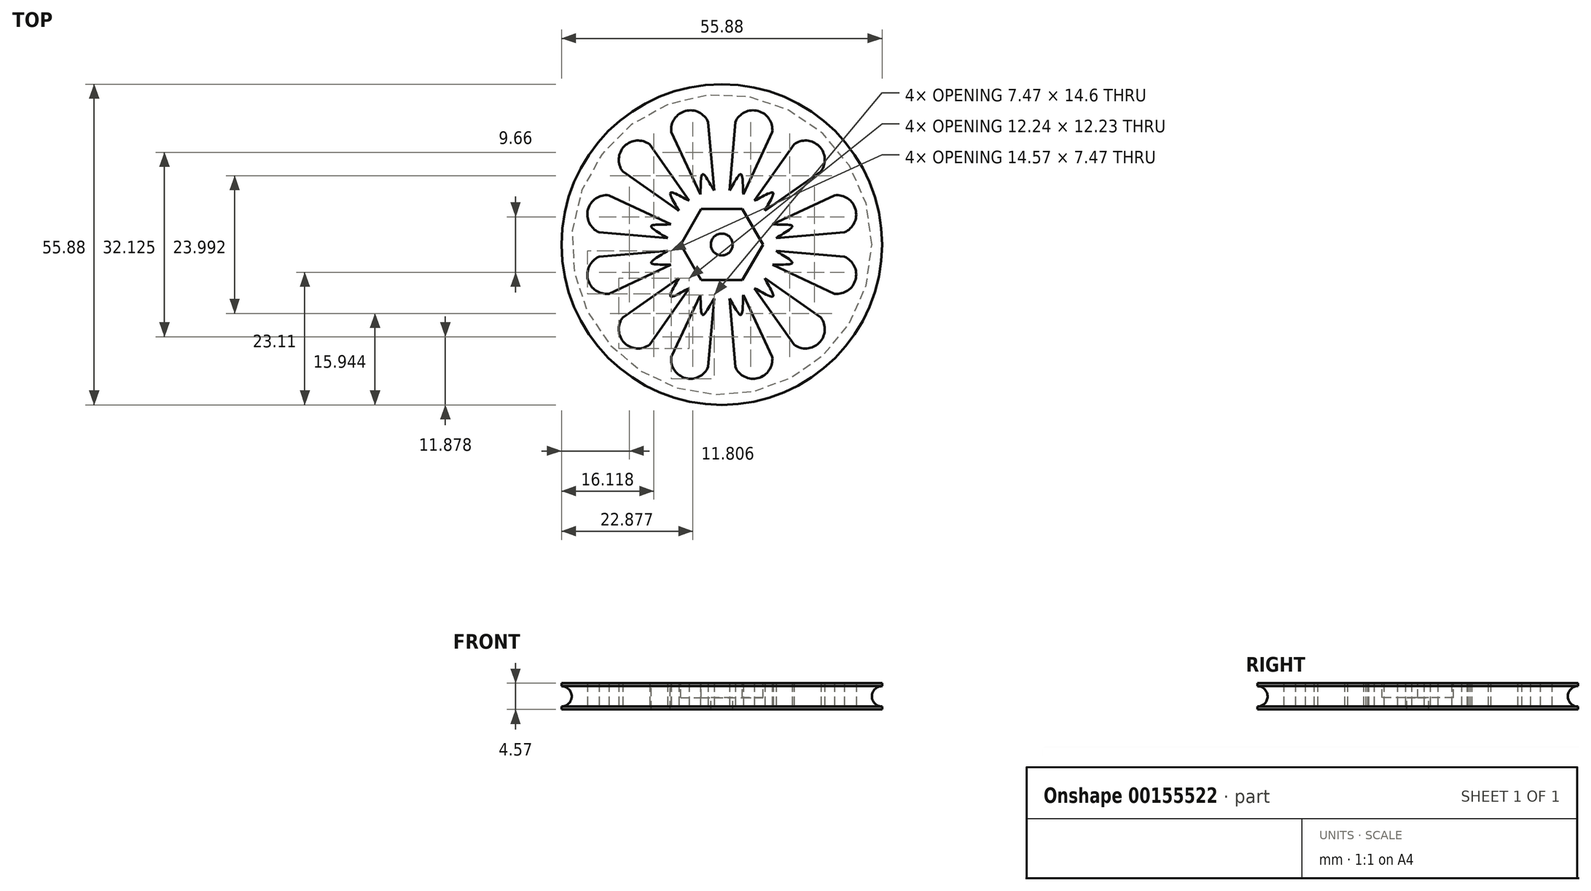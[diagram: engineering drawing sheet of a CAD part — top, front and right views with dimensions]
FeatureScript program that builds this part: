
annotation { "Feature Type Name" : "Feature", "Feature Type Description" : "" }
export const myFeature = defineFeature(function(context is Context, id is Id, definition is map)
    precondition{}
    {
        {
            var Q0;
            Q0=qCreatedBy(makeId("Top.planeOp"),FACE);
            var sketch = newSketch(context, id + "F0", { "sketchPlane" : qUnion([Q0])});
            skCircle(sketch, "E0", {"center": v(0, 0) * mm, "radius": 27.94 * mm});
            skLineSegment(sketch, "E1", {"start": v(-27.94, 0) * mm, "end": v(27.94, 0) * mm, "construction": true});
            skLineSegment(sketch, "E2", {"start": v(0, -27.94) * mm, "end": v(0, 27.94) * mm, "construction": true});
            skArc(sketch, "E3", {"start": v(2.37, 21.33) * mm, "mid": v(6.33, 23.27) * mm, "end": v(8.8, 19.6) * mm});
            skArc(sketch, "E4", {"start": v(12.57, 17.44) * mm, "mid": v(16.97, 17.13) * mm, "end": v(17.27, 12.73) * mm});
            skArc(sketch, "E5", {"start": v(19.67, 8.57) * mm, "mid": v(23.32, 6.1) * mm, "end": v(21.39, 2.14) * mm});
            skArc(sketch, "E6.MirrorCS", {"start": v(-2.37, 21.33) * mm, "mid": v(-6.33, 23.27) * mm, "end": v(-8.8, 19.6) * mm});
            skArc(sketch, "E7.MirrorCS", {"start": v(-12.57, 17.44) * mm, "mid": v(-16.97, 17.13) * mm, "end": v(-17.27, 12.73) * mm});
            skArc(sketch, "E8.MirrorCS", {"start": v(-19.67, 8.57) * mm, "mid": v(-23.32, 6.1) * mm, "end": v(-21.39, 2.14) * mm});
            skArc(sketch, "E9.MirrorCS", {"start": v(-19.67, -8.57) * mm, "mid": v(-23.32, -6.1) * mm, "end": v(-21.39, -2.14) * mm});
            skArc(sketch, "E10.MirrorCS", {"start": v(-12.57, -17.44) * mm, "mid": v(-16.97, -17.13) * mm, "end": v(-17.27, -12.73) * mm});
            skArc(sketch, "E11.MirrorCS", {"start": v(-2.37, -21.33) * mm, "mid": v(-6.33, -23.27) * mm, "end": v(-8.8, -19.6) * mm});
            skArc(sketch, "E12.MirrorCS", {"start": v(2.37, -21.33) * mm, "mid": v(6.33, -23.27) * mm, "end": v(8.8, -19.6) * mm});
            skArc(sketch, "E13.MirrorCS", {"start": v(12.57, -17.44) * mm, "mid": v(16.97, -17.13) * mm, "end": v(17.27, -12.73) * mm});
            skArc(sketch, "E14.MirrorCS", {"start": v(19.67, -8.57) * mm, "mid": v(23.32, -6.1) * mm, "end": v(21.39, -2.14) * mm});
            skCircle(sketch, "E15", {"center": v(0, 0) * mm, "radius": 6.99 * mm, "construction": true});
            skLineSegment(sketch, "E16.0", {"start": v(6.99, 0) * mm, "end": v(3.5, -6.05) * mm});
            skLineSegment(sketch, "E16.1", {"start": v(3.5, -6.05) * mm, "end": v(-3.5, -6.05) * mm});
            skLineSegment(sketch, "E16.2", {"start": v(-3.5, -6.05) * mm, "end": v(-6.99, 0) * mm});
            skLineSegment(sketch, "E16.3", {"start": v(-6.99, 0) * mm, "end": v(-3.5, 6.05) * mm});
            skLineSegment(sketch, "E16.4", {"start": v(-3.5, 6.05) * mm, "end": v(3.5, 6.05) * mm});
            skLineSegment(sketch, "E16.5", {"start": v(3.5, 6.05) * mm, "end": v(6.99, 0) * mm});
            skCircle(sketch, "E17", {"center": v(0, 0) * mm, "radius": 9.53 * mm, "construction": true});
            skLineSegment(sketch, "E18.trimOffspring", {"start": v(-3.74, 8.76) * mm, "end": v(-8.8, 19.6) * mm});
            skLineSegment(sketch, "E19.trimOffspring", {"start": v(-5.7, 7.63) * mm, "end": v(-12.57, 17.44) * mm});
            skLineSegment(sketch, "E20.trimOffspring", {"start": v(-7.5, 5.88) * mm, "end": v(-17.27, 12.73) * mm});
            skLineSegment(sketch, "E21.trimOffspring", {"start": v(-8.85, 3.52) * mm, "end": v(-19.67, 8.57) * mm});
            skLineSegment(sketch, "E22.trimOffspring", {"start": v(-9.46, 1.1) * mm, "end": v(-21.39, 2.14) * mm});
            skLineSegment(sketch, "E23.trimOffspring", {"start": v(-9.46, -1.1) * mm, "end": v(-21.39, -2.14) * mm});
            skLineSegment(sketch, "E24.trimOffspring", {"start": v(-8.85, -3.52) * mm, "end": v(-19.67, -8.57) * mm});
            skLineSegment(sketch, "E25.trimOffspring", {"start": v(-7.5, -5.88) * mm, "end": v(-17.27, -12.73) * mm});
            skLineSegment(sketch, "E26.trimOffspring", {"start": v(-5.7, -7.63) * mm, "end": v(-12.57, -17.44) * mm});
            skLineSegment(sketch, "E27.trimOffspring", {"start": v(-3.74, -8.76) * mm, "end": v(-8.8, -19.6) * mm});
            skLineSegment(sketch, "E28.trimOffspring", {"start": v(-1.33, -9.43) * mm, "end": v(-2.37, -21.33) * mm});
            skLineSegment(sketch, "E29.trimOffspring", {"start": v(1.33, -9.43) * mm, "end": v(2.37, -21.33) * mm});
            skLineSegment(sketch, "E30.trimOffspring", {"start": v(3.74, -8.76) * mm, "end": v(8.8, -19.6) * mm});
            skLineSegment(sketch, "E31.trimOffspring", {"start": v(5.7, -7.63) * mm, "end": v(12.57, -17.44) * mm});
            skLineSegment(sketch, "E32.trimOffspring", {"start": v(7.5, -5.88) * mm, "end": v(17.27, -12.73) * mm});
            skLineSegment(sketch, "E33.trimOffspring", {"start": v(8.85, -3.52) * mm, "end": v(19.67, -8.57) * mm});
            skLineSegment(sketch, "E34.trimOffspring", {"start": v(9.46, -1.1) * mm, "end": v(21.39, -2.14) * mm});
            skLineSegment(sketch, "E35.trimOffspring", {"start": v(9.46, 1.1) * mm, "end": v(21.39, 2.14) * mm});
            skLineSegment(sketch, "E36.trimOffspring", {"start": v(8.85, 3.52) * mm, "end": v(19.67, 8.57) * mm});
            skLineSegment(sketch, "E37.trimOffspring", {"start": v(7.5, 5.88) * mm, "end": v(17.27, 12.73) * mm});
            skLineSegment(sketch, "E38.trimOffspring", {"start": v(5.7, 7.63) * mm, "end": v(12.57, 17.44) * mm});
            skLineSegment(sketch, "E39.trimOffspring", {"start": v(3.74, 8.76) * mm, "end": v(8.8, 19.6) * mm});
            skLineSegment(sketch, "E40.trimOffspring", {"start": v(1.33, 9.43) * mm, "end": v(2.37, 21.33) * mm});
            skLineSegment(sketch, "E41.trimOffspring", {"start": v(-1.33, 9.43) * mm, "end": v(-2.37, 21.33) * mm});
            skLineSegment(sketch, "E42", {"start": v(5.46, 20.02) * mm, "end": v(0, 0) * mm, "construction": true});
            skLineSegment(sketch, "E43", {"start": v(0, 0) * mm, "end": v(14.6, 14.76) * mm, "construction": true});
            skLineSegment(sketch, "E44", {"start": v(20.07, 5.23) * mm, "end": v(0, 0) * mm, "construction": true});
            skCircle(sketch, "E45", {"center": v(0, 0) * mm, "radius": 12.7 * mm, "construction": true});
            skFitSpline(sketch, "E46", {"points": [v(1.33, 9.43) * mm, v(3.34, 12.25) * mm, v(3.74, 8.76) * mm], "startDerivative": vector(4.33, 6.63) * mm, "endDerivative": vector(0.64, -7.98) * mm});
            skFitSpline(sketch, "E47", {"points": [v(5.7, 7.63) * mm, v(8.93, 9.03) * mm, v(7.5, 5.88) * mm], "startDerivative": vector(7.24, 3.44) * mm, "endDerivative": vector(-3.58, -7.06) * mm});
            skFitSpline(sketch, "E48", {"points": [v(8.85, 3.52) * mm, v(12.29, 3.2) * mm, v(9.46, 1.1) * mm], "startDerivative": vector(7.9, -0.42) * mm, "endDerivative": vector(-6.6, -4.55) * mm});
            skFitSpline(sketch, "E49.MirrorCS", {"points": [v(-1.33, 9.43) * mm, v(-3.34, 12.25) * mm, v(-3.74, 8.76) * mm], "startDerivative": vector(-4.33, 6.63) * mm, "endDerivative": vector(-0.64, -7.98) * mm});
            skFitSpline(sketch, "E50.MirrorCS", {"points": [v(-5.7, 7.63) * mm, v(-8.93, 9.03) * mm, v(-7.5, 5.88) * mm], "startDerivative": vector(-7.24, 3.44) * mm, "endDerivative": vector(3.58, -7.06) * mm});
            skFitSpline(sketch, "E51.MirrorCS", {"points": [v(-8.85, 3.52) * mm, v(-12.29, 3.2) * mm, v(-9.46, 1.1) * mm], "startDerivative": vector(-7.9, -0.42) * mm, "endDerivative": vector(6.6, -4.55) * mm});
            skFitSpline(sketch, "E52.MirrorCS", {"points": [v(-8.85, -3.52) * mm, v(-12.29, -3.2) * mm, v(-9.46, -1.1) * mm], "startDerivative": vector(-7.9, 0.42) * mm, "endDerivative": vector(6.6, 4.55) * mm});
            skFitSpline(sketch, "E53.MirrorCS", {"points": [v(-5.7, -7.63) * mm, v(-8.93, -9.03) * mm, v(-7.5, -5.88) * mm], "startDerivative": vector(-7.24, -3.44) * mm, "endDerivative": vector(3.58, 7.06) * mm});
            skFitSpline(sketch, "E54.MirrorCS", {"points": [v(-1.33, -9.43) * mm, v(-3.34, -12.25) * mm, v(-3.74, -8.76) * mm], "startDerivative": vector(-4.33, -6.63) * mm, "endDerivative": vector(-0.64, 7.98) * mm});
            skFitSpline(sketch, "E55.MirrorCS", {"points": [v(1.33, -9.43) * mm, v(3.34, -12.25) * mm, v(3.74, -8.76) * mm], "startDerivative": vector(4.33, -6.63) * mm, "endDerivative": vector(0.64, 7.98) * mm});
            skFitSpline(sketch, "E56.MirrorCS", {"points": [v(5.7, -7.63) * mm, v(8.93, -9.03) * mm, v(7.5, -5.88) * mm], "startDerivative": vector(7.24, -3.44) * mm, "endDerivative": vector(-3.58, 7.06) * mm});
            skFitSpline(sketch, "E57.MirrorCS", {"points": [v(8.85, -3.52) * mm, v(12.29, -3.2) * mm, v(9.46, -1.1) * mm], "startDerivative": vector(7.9, 0.42) * mm, "endDerivative": vector(-6.6, 4.55) * mm});
            skSolve(sketch);
        }
        {
            var Q0;
            Q0=makeQuery(id+"F0.imprint","IMPRINT",FACE,{"disambiguationData":[TD([[makeQuery(id+"F0.imprint","IMPRINT",EDGE,{"derivedFrom":sQuery(id+"F0.wireOp",EDGE,"E0")}),1.0]])]});
            var Q1;
            {var subQ0=sQuery(id+"F0.wireOp",EDGE,"E17");var subQ10=makeQuery(id+"F0.imprint","INTERSECT",VERTEX,{"derivedFrom":[subQ0,sQuery(id+"F0.wireOp",EDGE,"E35.trimOffspring")]});Q1=makeQuery(id+"F0.imprint","IMPRINT",FACE,{"disambiguationData":[TD([[makeQuery(id+"F0.imprint","IMPRINT",EDGE,{"disambiguationData":[TD([[subQ10,-1.0]])],"derivedFrom":subQ0}),1.0]])]});}
            var Q2;
            {var subQ0=sQuery(id+"F0.wireOp",EDGE,"E16.3");Q2=makeQuery(id+"F0.imprint","IMPRINT",FACE,{"disambiguationData":[TD([[makeQuery(id+"F0.imprint","IMPRINT",EDGE,{"derivedFrom":subQ0}),1.0]])]});}
            var Q3;
            {var subQ0=sQuery(id+"F0.wireOp",EDGE,"E16.2");Q3=makeQuery(id+"F0.imprint","IMPRINT",FACE,{"disambiguationData":[TD([[makeQuery(id+"F0.imprint","IMPRINT",EDGE,{"derivedFrom":subQ0}),1.0]])]});}
            var Q4;
            {var subQ0=sQuery(id+"F0.wireOp",EDGE,"E16.4");Q4=makeQuery(id+"F0.imprint","IMPRINT",FACE,{"disambiguationData":[TD([[makeQuery(id+"F0.imprint","IMPRINT",EDGE,{"derivedFrom":subQ0}),1.0]])]});}
            var Q5;
            {var subQ0=sQuery(id+"F0.wireOp",EDGE,"E16.5");Q5=makeQuery(id+"F0.imprint","IMPRINT",FACE,{"disambiguationData":[TD([[makeQuery(id+"F0.imprint","IMPRINT",EDGE,{"derivedFrom":subQ0}),1.0]])]});}
            var Q6;
            {var subQ0=sQuery(id+"F0.wireOp",EDGE,"E16.0");Q6=makeQuery(id+"F0.imprint","IMPRINT",FACE,{"disambiguationData":[TD([[makeQuery(id+"F0.imprint","IMPRINT",EDGE,{"derivedFrom":subQ0}),1.0]])]});}
            var Q7;
            {var subQ0=sQuery(id+"F0.wireOp",EDGE,"E16.1");Q7=makeQuery(id+"F0.imprint","IMPRINT",FACE,{"disambiguationData":[TD([[makeQuery(id+"F0.imprint","IMPRINT",EDGE,{"derivedFrom":subQ0}),1.0]])]});}
            var Q8;
            Q8=makeQuery(id+"F0.imprint","IMPRINT",FACE,{"disambiguationData":[TD([[makeQuery(id+"F0.imprint","IMPRINT",EDGE,{"derivedFrom":sQuery(id+"F0.wireOp",EDGE,"E16.0")}),-1.0]])]});
            extrude(context, id + "F1", {"entities" : qUnion([Q0, Q1, Q2, Q3, Q4, Q5, Q6, Q7, Q8]), "depth" : 4.57 * mm});
        }
        {
            var Q0;
            Q0=qCreatedBy(makeId("Front.planeOp"),FACE);
            var sketch = newSketch(context, id + "F2", { "sketchPlane" : qUnion([Q0])});
            skLineSegment(sketch, "E58", {"start": v(0, 0) * mm, "end": v(0, 4.57) * mm, "construction": true});
            skLineSegment(sketch, "E59", {"start": v(0, 0) * mm, "end": v(27.94, 0) * mm, "construction": true});
            skLineSegment(sketch, "E60", {"start": v(27.94, 0) * mm, "end": v(27.94, 4.57) * mm, "construction": true});
            skLineSegment(sketch, "E61", {"start": v(27.94, 4.57) * mm, "end": v(0, 4.57) * mm, "construction": true});
            skArc(sketch, "E62", {"start": v(27.94, 4.06) * mm, "mid": v(26.16, 2.29) * mm, "end": v(27.94, 0.5) * mm});
            skLineSegment(sketch, "E63", {"start": v(27.94, 4.06) * mm, "end": v(27.94, 0.5) * mm});
            skSolve(sketch);
        }
        {
            var Q0;
            Q0 = qSketchRegion(id + "F2", true);
            var Q1;
            Q1=sQuery(id+"F2.wireOp",EDGE,"E58");
            revolve(context, id + "F3", {"operationType" : NewBodyOperationType.REMOVE, "entities" : qUnion([Q0]), "axis" : qUnion([Q1]), "revolveType" : RevolveType.FULL, "oppositeDirection" : true});
        }
        {
            var Q0;
            Q0=makeQuery(id+"F1.opExtrude","CAP_FACE",FACE,{"disambiguationData":[OSD([sQuery(id+"F0.wireOp",EDGE,"E0"),sQuery(id+"F0.wireOp",EDGE,"E3"),sQuery(id+"F0.wireOp",EDGE,"E4"),sQuery(id+"F0.wireOp",EDGE,"E5"),sQuery(id+"F0.wireOp",EDGE,"E6.MirrorCS"),sQuery(id+"F0.wireOp",EDGE,"E7.MirrorCS"),sQuery(id+"F0.wireOp",EDGE,"E8.MirrorCS"),sQuery(id+"F0.wireOp",EDGE,"E9.MirrorCS"),sQuery(id+"F0.wireOp",EDGE,"E10.MirrorCS"),sQuery(id+"F0.wireOp",EDGE,"E11.MirrorCS"),sQuery(id+"F0.wireOp",EDGE,"E12.MirrorCS"),sQuery(id+"F0.wireOp",EDGE,"E13.MirrorCS"),sQuery(id+"F0.wireOp",EDGE,"E14.MirrorCS"),sQuery(id+"F0.wireOp",EDGE,"E18.trimOffspring"),sQuery(id+"F0.wireOp",EDGE,"E19.trimOffspring"),sQuery(id+"F0.wireOp",EDGE,"E20.trimOffspring"),sQuery(id+"F0.wireOp",EDGE,"E21.trimOffspring"),sQuery(id+"F0.wireOp",EDGE,"E22.trimOffspring"),sQuery(id+"F0.wireOp",EDGE,"E23.trimOffspring"),sQuery(id+"F0.wireOp",EDGE,"E24.trimOffspring"),sQuery(id+"F0.wireOp",EDGE,"E25.trimOffspring"),sQuery(id+"F0.wireOp",EDGE,"E26.trimOffspring"),sQuery(id+"F0.wireOp",EDGE,"E27.trimOffspring"),sQuery(id+"F0.wireOp",EDGE,"E28.trimOffspring"),sQuery(id+"F0.wireOp",EDGE,"E29.trimOffspring"),sQuery(id+"F0.wireOp",EDGE,"E30.trimOffspring"),sQuery(id+"F0.wireOp",EDGE,"E31.trimOffspring"),sQuery(id+"F0.wireOp",EDGE,"E32.trimOffspring"),sQuery(id+"F0.wireOp",EDGE,"E33.trimOffspring"),sQuery(id+"F0.wireOp",EDGE,"E34.trimOffspring"),sQuery(id+"F0.wireOp",EDGE,"E35.trimOffspring"),sQuery(id+"F0.wireOp",EDGE,"E36.trimOffspring"),sQuery(id+"F0.wireOp",EDGE,"E37.trimOffspring"),sQuery(id+"F0.wireOp",EDGE,"E38.trimOffspring"),sQuery(id+"F0.wireOp",EDGE,"E39.trimOffspring"),sQuery(id+"F0.wireOp",EDGE,"E40.trimOffspring"),sQuery(id+"F0.wireOp",EDGE,"E41.trimOffspring"),sQuery(id+"F0.wireOp",EDGE,"E46"),sQuery(id+"F0.wireOp",EDGE,"E47"),sQuery(id+"F0.wireOp",EDGE,"E48"),sQuery(id+"F0.wireOp",EDGE,"E49.MirrorCS"),sQuery(id+"F0.wireOp",EDGE,"E50.MirrorCS"),sQuery(id+"F0.wireOp",EDGE,"E51.MirrorCS"),sQuery(id+"F0.wireOp",EDGE,"E52.MirrorCS"),sQuery(id+"F0.wireOp",EDGE,"E53.MirrorCS"),sQuery(id+"F0.wireOp",EDGE,"E54.MirrorCS"),sQuery(id+"F0.wireOp",EDGE,"E55.MirrorCS"),sQuery(id+"F0.wireOp",EDGE,"E56.MirrorCS"),sQuery(id+"F0.wireOp",EDGE,"E57.MirrorCS")])],"isStart":false});
            var sketch = newSketch(context, id + "F4", { "sketchPlane" : qUnion([Q0])});
            skCircle(sketch, "E64", {"center": v(0, 0) * mm, "radius": 7.18 * mm, "construction": true});
            skLineSegment(sketch, "E65.0", {"start": v(7.18, 0) * mm, "end": v(3.59, -6.21) * mm});
            skLineSegment(sketch, "E65.1", {"start": v(3.59, -6.21) * mm, "end": v(-3.59, -6.21) * mm});
            skLineSegment(sketch, "E65.2", {"start": v(-3.59, -6.21) * mm, "end": v(-7.18, 0) * mm});
            skLineSegment(sketch, "E65.3", {"start": v(-7.18, 0) * mm, "end": v(-3.59, 6.21) * mm});
            skLineSegment(sketch, "E65.4", {"start": v(-3.59, 6.21) * mm, "end": v(3.59, 6.21) * mm});
            skLineSegment(sketch, "E65.5", {"start": v(3.59, 6.21) * mm, "end": v(7.18, 0) * mm});
            skSolve(sketch);
        }
        {
            var Q0;
            Q0 = qSketchRegion(id + "F4", true);
            extrude(context, id + "F5", {"entities" : qUnion([Q0]), "operationType" : NewBodyOperationType.REMOVE, "oppositeDirection" : true, "depth" : 2.54 * mm});
        }
        {
            var Q0;
            Q0=makeQuery(id+"F5.boolean.opBoolean","COPY",FACE,{"derivedFrom":makeQuery(id+"F5.opExtrude","CAP_FACE",FACE,{"disambiguationData":[OSD([sQuery(id+"F4.wireOp",EDGE,"E65.0"),sQuery(id+"F4.wireOp",EDGE,"E65.1"),sQuery(id+"F4.wireOp",EDGE,"E65.2"),sQuery(id+"F4.wireOp",EDGE,"E65.3"),sQuery(id+"F4.wireOp",EDGE,"E65.4"),sQuery(id+"F4.wireOp",EDGE,"E65.5")])],"isStart":false})});
            var sketch = newSketch(context, id + "F6", { "sketchPlane" : qUnion([Q0])});
            skPoint(sketch, "E66", {"position": v(0, 0) * mm});
            skSolve(sketch);
        }
        {
            var Q0;
            Q0=sQuery(id+"F6.wireOp",VERTEX,"E66");
            var Q1;
            Q1=makeQuery(id+"F1.opExtrude","SWEPT_BODY",BODY,{"disambiguationData":[OSD([sQuery(id+"F0.wireOp",EDGE,"E0"),sQuery(id+"F0.wireOp",EDGE,"E3"),sQuery(id+"F0.wireOp",EDGE,"E4"),sQuery(id+"F0.wireOp",EDGE,"E5"),sQuery(id+"F0.wireOp",EDGE,"E6.MirrorCS"),sQuery(id+"F0.wireOp",EDGE,"E7.MirrorCS"),sQuery(id+"F0.wireOp",EDGE,"E8.MirrorCS"),sQuery(id+"F0.wireOp",EDGE,"E9.MirrorCS"),sQuery(id+"F0.wireOp",EDGE,"E10.MirrorCS"),sQuery(id+"F0.wireOp",EDGE,"E11.MirrorCS"),sQuery(id+"F0.wireOp",EDGE,"E12.MirrorCS"),sQuery(id+"F0.wireOp",EDGE,"E13.MirrorCS"),sQuery(id+"F0.wireOp",EDGE,"E14.MirrorCS"),sQuery(id+"F0.wireOp",EDGE,"E18.trimOffspring"),sQuery(id+"F0.wireOp",EDGE,"E19.trimOffspring"),sQuery(id+"F0.wireOp",EDGE,"E20.trimOffspring"),sQuery(id+"F0.wireOp",EDGE,"E21.trimOffspring"),sQuery(id+"F0.wireOp",EDGE,"E22.trimOffspring"),sQuery(id+"F0.wireOp",EDGE,"E23.trimOffspring"),sQuery(id+"F0.wireOp",EDGE,"E24.trimOffspring"),sQuery(id+"F0.wireOp",EDGE,"E25.trimOffspring"),sQuery(id+"F0.wireOp",EDGE,"E26.trimOffspring"),sQuery(id+"F0.wireOp",EDGE,"E27.trimOffspring"),sQuery(id+"F0.wireOp",EDGE,"E28.trimOffspring"),sQuery(id+"F0.wireOp",EDGE,"E29.trimOffspring"),sQuery(id+"F0.wireOp",EDGE,"E30.trimOffspring"),sQuery(id+"F0.wireOp",EDGE,"E31.trimOffspring"),sQuery(id+"F0.wireOp",EDGE,"E32.trimOffspring"),sQuery(id+"F0.wireOp",EDGE,"E33.trimOffspring"),sQuery(id+"F0.wireOp",EDGE,"E34.trimOffspring"),sQuery(id+"F0.wireOp",EDGE,"E35.trimOffspring"),sQuery(id+"F0.wireOp",EDGE,"E36.trimOffspring"),sQuery(id+"F0.wireOp",EDGE,"E37.trimOffspring"),sQuery(id+"F0.wireOp",EDGE,"E38.trimOffspring"),sQuery(id+"F0.wireOp",EDGE,"E39.trimOffspring"),sQuery(id+"F0.wireOp",EDGE,"E40.trimOffspring"),sQuery(id+"F0.wireOp",EDGE,"E41.trimOffspring"),sQuery(id+"F0.wireOp",EDGE,"E46"),sQuery(id+"F0.wireOp",EDGE,"E47"),sQuery(id+"F0.wireOp",EDGE,"E48"),sQuery(id+"F0.wireOp",EDGE,"E49.MirrorCS"),sQuery(id+"F0.wireOp",EDGE,"E50.MirrorCS"),sQuery(id+"F0.wireOp",EDGE,"E51.MirrorCS"),sQuery(id+"F0.wireOp",EDGE,"E52.MirrorCS"),sQuery(id+"F0.wireOp",EDGE,"E53.MirrorCS"),sQuery(id+"F0.wireOp",EDGE,"E54.MirrorCS"),sQuery(id+"F0.wireOp",EDGE,"E55.MirrorCS"),sQuery(id+"F0.wireOp",EDGE,"E56.MirrorCS"),sQuery(id+"F0.wireOp",EDGE,"E57.MirrorCS")])]});
            hole(context, id + "F7", {"style" : HoleStyle.SIMPLE, "endStyle" : HoleEndStyle.THROUGH, "holeDiameter" : 3.8 * mm, "locations" : qUnion([Q0]), "scope" : qUnion([Q1]), "isTappedThrough" : true});
        }
    });
